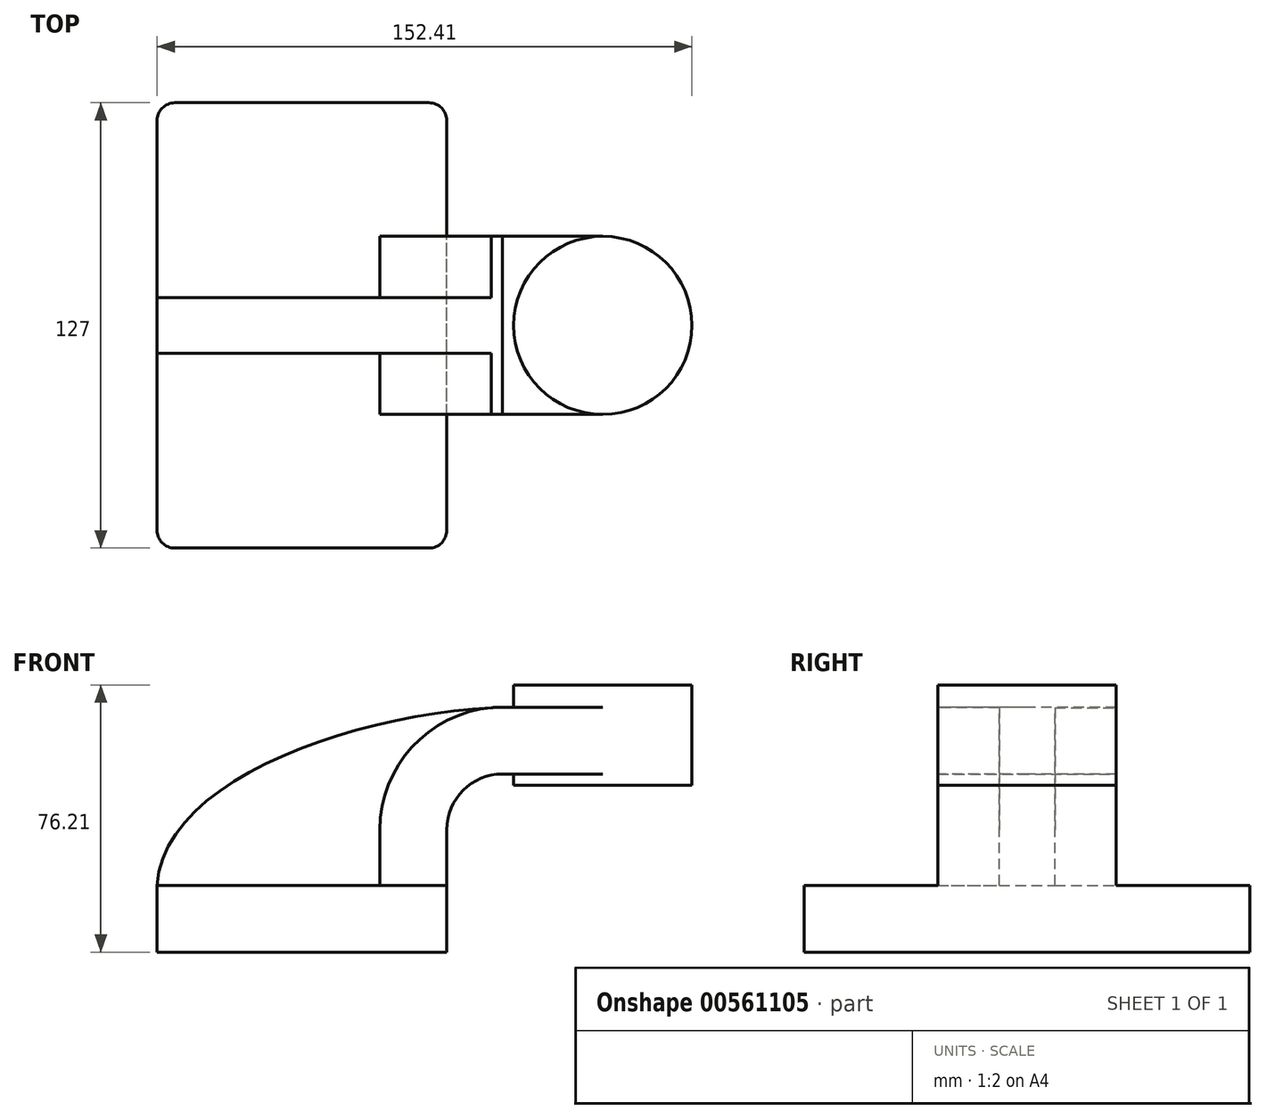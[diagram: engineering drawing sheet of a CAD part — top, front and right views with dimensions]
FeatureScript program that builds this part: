
annotation { "Feature Type Name" : "Feature", "Feature Type Description" : "" }
export const myFeature = defineFeature(function(context is Context, id is Id, definition is map)
    precondition{}
    {
        {
            var Q0;
            Q0=qCreatedBy(makeId("Front.planeOp"),FACE);
            var sketch = newSketch(context, id + "F0", { "sketchPlane" : qUnion([Q0])});
            skLineSegment(sketch, "E0.rect.bottom", {"start": v(-41.28, 9.52) * mm, "end": v(41.28, 9.52) * mm});
            skLineSegment(sketch, "E0.rect.top", {"start": v(-41.28, -9.52) * mm, "end": v(41.28, -9.52) * mm});
            skLineSegment(sketch, "E0.rect.left", {"start": v(-41.28, 9.52) * mm, "end": v(-41.28, -9.52) * mm});
            skLineSegment(sketch, "E0.rect.right", {"start": v(41.28, 9.52) * mm, "end": v(41.28, -9.52) * mm});
            skPoint(sketch, "E0.rect.middle", {"position": v(0, 0) * mm});
            skLineSegment(sketch, "E1", {"start": v(41.28, 9.52) * mm, "end": v(41.28, 25.4) * mm});
            skArc(sketch, "E2", {"start": v(41.27, 25.4) * mm, "mid": v(45.92, 36.63) * mm, "end": v(57.15, 41.28) * mm});
            skLineSegment(sketch, "E3", {"start": v(57.15, 41.28) * mm, "end": v(85.72, 41.28) * mm});
            skLineSegment(sketch, "E4.rect.bottom", {"start": v(60.32, 38.1) * mm, "end": v(111.13, 38.1) * mm});
            skLineSegment(sketch, "E4.rect.top", {"start": v(60.32, 66.68) * mm, "end": v(111.12, 66.68) * mm});
            skLineSegment(sketch, "E4.rect.left", {"start": v(60.32, 38.1) * mm, "end": v(60.32, 66.68) * mm});
            skLineSegment(sketch, "E4.rect.right", {"start": v(111.13, 38.1) * mm, "end": v(111.12, 66.68) * mm});
            skPoint(sketch, "E4.rect.middle", {"position": v(85.72, 52.39) * mm});
            skLineSegment(sketch, "E5.0", {"start": v(57.15, 60.33) * mm, "end": v(85.72, 60.33) * mm});
            skArc(sketch, "E5.1", {"start": v(22.23, 25.4) * mm, "mid": v(32.45, 50.1) * mm, "end": v(57.15, 60.33) * mm});
            skLineSegment(sketch, "E5.2", {"start": v(22.23, 9.52) * mm, "end": v(22.23, 25.4) * mm});
            skLineSegment(sketch, "E6", {"start": v(85.72, 38.1) * mm, "end": v(85.72, 66.68) * mm});
            skFitSpline(sketch, "E7", {"points": [v(-41.28, 9.53) * mm, v(57.15, 60.33) * mm], "startDerivative": vector(5.2, 92.34) * mm, "endDerivative": vector(120.92, 4.22) * mm});
            skSolve(sketch);
        }
        {
            var Q0;
            Q0=makeQuery(id+"F0.imprint","IMPRINT",FACE,{"disambiguationData":[TD([[makeQuery(id+"F0.imprint","IMPRINT",EDGE,{"derivedFrom":sQuery(id+"F0.wireOp",EDGE,"E0.rect.top")}),1.0]])]});
            extrude(context, id + "F1", {"entities" : qUnion([Q0]), "endBound" : BoundingType.SYMMETRIC, "depth" : 127 * mm, "offsetDistance" : 25.4 * mm});
        }
        {
            var Q0;
            {var subQ9=sQuery(id+"F0.wireOp",EDGE,"E1");Q0=makeQuery(id+"F0.imprint","IMPRINT",FACE,{"disambiguationData":[TD([[makeQuery(id+"F0.imprint","IMPRINT",EDGE,{"derivedFrom":subQ9}),1.0]])]});}
            var Q1;
            {var subQ0=sQuery(id+"F0.wireOp",EDGE,"E6");var subQ1=sQuery(id+"F0.wireOp",EDGE,"E3");var subQ2=makeQuery(id+"F0.imprint","INTERSECT",VERTEX,{"derivedFrom":[subQ1,subQ0]});Q1=makeQuery(id+"F0.imprint","IMPRINT",FACE,{"disambiguationData":[TD([[makeQuery(id+"F0.imprint","IMPRINT",EDGE,{"disambiguationData":[TD([[subQ2,1.0]])],"derivedFrom":subQ1}),1.0]])]});}
            extrude(context, id + "F2", {"entities" : qUnion([Q0, Q1]), "operationType" : NewBodyOperationType.ADD, "endBound" : BoundingType.SYMMETRIC, "depth" : 50.8 * mm});
        }
        {
            var Q0;
            {var subQ3=sQuery(id+"F0.wireOp",EDGE,"E5.2");Q0=makeQuery(id+"F0.imprint","IMPRINT",FACE,{"disambiguationData":[TD([[makeQuery(id+"F0.imprint","IMPRINT",EDGE,{"derivedFrom":subQ3}),1.0]])]});}
            extrude(context, id + "F3", {"entities" : qUnion([Q0]), "operationType" : NewBodyOperationType.ADD, "endBound" : BoundingType.SYMMETRIC, "depth" : 15.88 * mm});
        }
        {
            var Q0;
            {var subQ5=sQuery(id+"F0.wireOp",EDGE,"E4.rect.right");Q0=makeQuery(id+"F0.imprint","IMPRINT",FACE,{"disambiguationData":[TD([[makeQuery(id+"F0.imprint","IMPRINT",EDGE,{"derivedFrom":subQ5}),1.0]])]});}
            var Q1;
            Q1=sQuery(id+"F0.wireOp",EDGE,"E6");
            revolve(context, id + "F4", {"operationType" : NewBodyOperationType.ADD, "entities" : qUnion([Q0]), "axis" : qUnion([Q1]), "revolveType" : RevolveType.FULL});
        }
        {
            var Q0;
            Q0=makeQuery(id+"F1.opExtrude","CAP_EDGE",EDGE,{"disambiguationData":[OSD([sQuery(id+"F0.wireOp",EDGE,"E0.rect.right")])],"isStart":false});
            var Q1;
            Q1=makeQuery(id+"F1.opExtrude","CAP_EDGE",EDGE,{"disambiguationData":[OSD([sQuery(id+"F0.wireOp",EDGE,"E0.rect.left")])],"isStart":false});
            var Q2;
            Q2=makeQuery(id+"F1.opExtrude","CAP_EDGE",EDGE,{"disambiguationData":[OSD([sQuery(id+"F0.wireOp",EDGE,"E0.rect.right")])],"isStart":true});
            var Q3;
            Q3=makeQuery(id+"F1.opExtrude","CAP_EDGE",EDGE,{"disambiguationData":[OSD([sQuery(id+"F0.wireOp",EDGE,"E0.rect.left")])],"isStart":true});
            fillet(context, id + "F5", {"entities" : qUnion([Q0, Q1, Q2, Q3]), "radius" : 5.08 * mm, "tangentPropagation" : true, "allowEdgeOverflow" : false});
        }
    });
